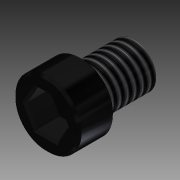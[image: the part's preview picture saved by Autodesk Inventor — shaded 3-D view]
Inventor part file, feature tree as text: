
AUTODESK INVENTOR PART (.ipt)
format: ipt  version: 2013 (Build 170138000, 138)  size: 116,224 bytes
history: native  units: in
note: dims shown in document units (in); Inventor stores cm internally (conversion verified against a paired STEP export)
features: extrude x3, sketch x1, thread x1, chamfer x1
ambient origin geometry x8: Origin, YZ Plane, XZ Plane, XY Plane, X Axis, Y Axis, Z Axis, Center Point
bodies: Solid1 (feature_tree)
feature tree (6):
  sketch  "Sketch1"  dims[d0=0.275in d1=0.185in d2=0.15in d3=0.15in d4=0.0in d5=0.215in d6=0.0in d7=0.05in d8=0.0in d9=1.0in d10=0.0in d11=0.01in d12=0.125in d13=45.0deg]
  extrude  "Extrusion1"  Depth=0.185in
  extrude  "Extrusion2"  Depth=0.15in
  extrude  "Extrusion3"  Depth=0.15in TaperAngle=0.0deg
  thread  "Thread1"  [1 undecoded]
  chamfer  "Chamfer1"  Distance=0.05in
note: 1 required parameter value undecoded (feature->parameter linkage not recoverable at this tier; creation-order binding heuristic only, values carry confidence <= 0.55)
